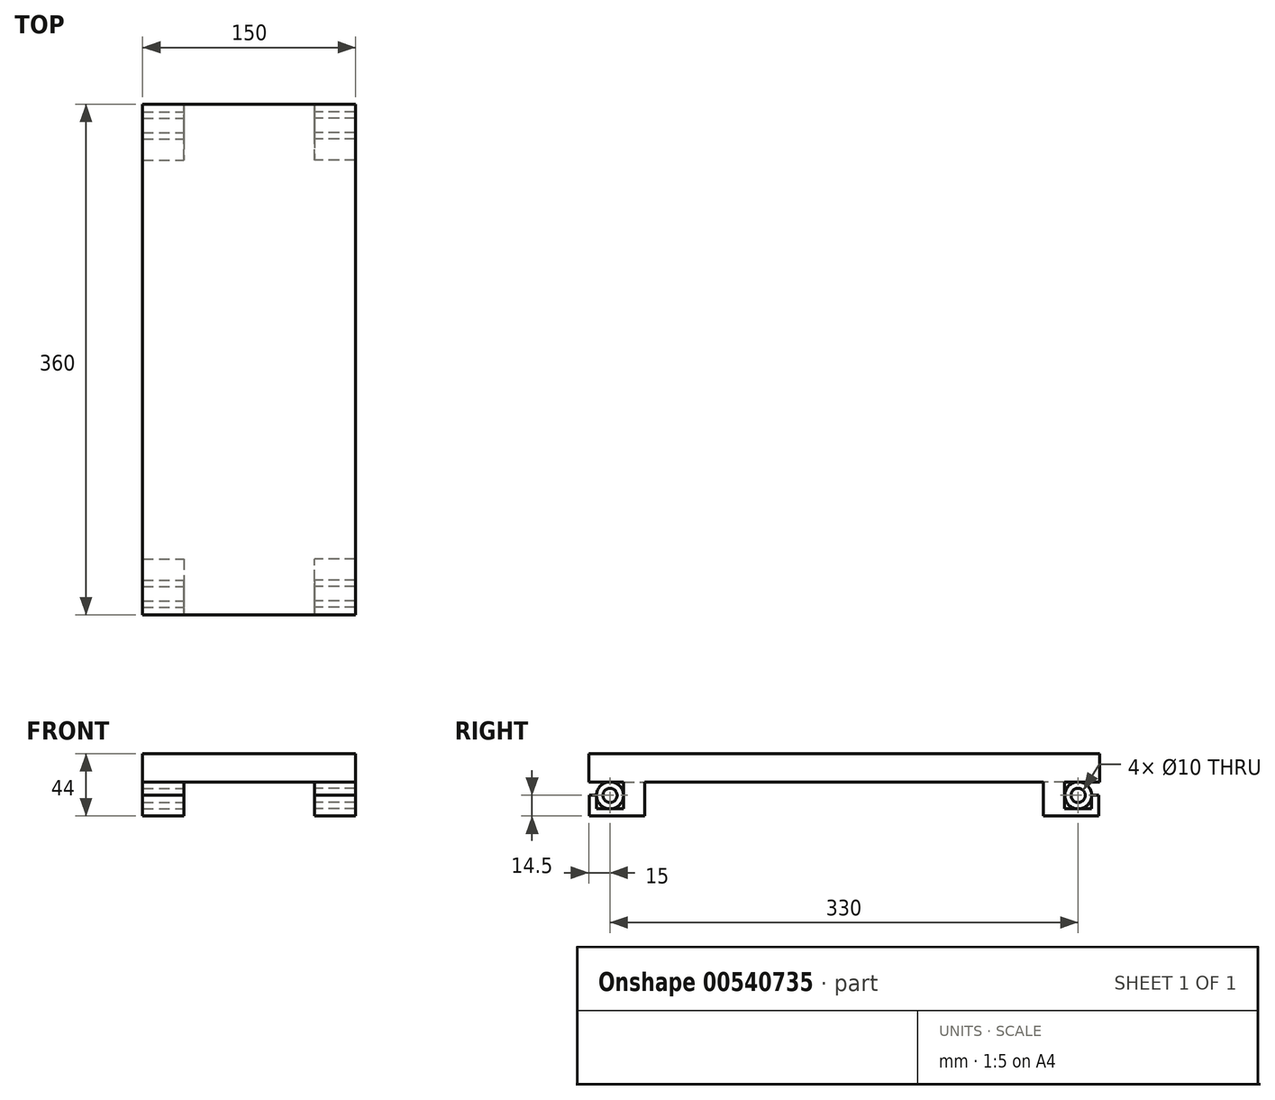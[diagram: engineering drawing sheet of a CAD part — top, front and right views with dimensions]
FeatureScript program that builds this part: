
annotation { "Feature Type Name" : "Feature", "Feature Type Description" : "" }
export const myFeature = defineFeature(function(context is Context, id is Id, definition is map)
    precondition{}
    {
        {
            var Q0;
            Q0=qCreatedBy(makeId("Right.planeOp"),FACE);
            var sketch = newSketch(context, id + "F0", { "sketchPlane" : qUnion([Q0])});
            skLineSegment(sketch, "E0.bottom", {"start": v(-180, 0) * mm, "end": v(180, 0) * mm});
            skLineSegment(sketch, "E0.top", {"start": v(-180, -20) * mm, "end": v(180, -20) * mm});
            skLineSegment(sketch, "E0.left", {"start": v(-180, 0) * mm, "end": v(-180, -20) * mm});
            skLineSegment(sketch, "E0.right", {"start": v(180, 0) * mm, "end": v(180, -20) * mm});
            skCircle(sketch, "E1", {"center": v(-165, -29.5) * mm, "radius": 9.5 * mm});
            skLineSegment(sketch, "E2", {"start": v(-165, -29.5) * mm, "end": v(165, -29.5) * mm, "construction": true});
            skCircle(sketch, "E3", {"center": v(165, -29.5) * mm, "radius": 9.5 * mm});
            skCircle(sketch, "E4", {"center": v(-165, -29.5) * mm, "radius": 5 * mm});
            skCircle(sketch, "E5", {"center": v(165, -29.5) * mm, "radius": 5 * mm});
            skPoint(sketch, "E6", {"position": v(0, 0) * mm});
            skLineSegment(sketch, "E7", {"start": v(-174.5, -29.5) * mm, "end": v(-179.5, -29.5) * mm});
            skLineSegment(sketch, "E8", {"start": v(-179.5, -29.5) * mm, "end": v(-179.5, -44) * mm});
            skLineSegment(sketch, "E9", {"start": v(-179.5, -44) * mm, "end": v(-140.5, -44) * mm});
            skLineSegment(sketch, "E10", {"start": v(-140.5, -44) * mm, "end": v(-140.5, -20) * mm});
            skLineSegment(sketch, "E11", {"start": v(-155.5, -20) * mm, "end": v(-155.5, -39) * mm});
            skLineSegment(sketch, "E12", {"start": v(-155.5, -39) * mm, "end": v(-174.5, -39) * mm});
            skLineSegment(sketch, "E13", {"start": v(-174.5, -39) * mm, "end": v(-174.5, -29.5) * mm});
            skPoint(sketch, "E14", {"position": v(0, -29.5) * mm});
            skLineSegment(sketch, "E15", {"start": v(0, 0) * mm, "end": v(0, -42.12) * mm, "construction": true});
            skLineSegment(sketch, "E16.MirrorCS", {"start": v(140.5, -44) * mm, "end": v(140.5, -20) * mm});
            skLineSegment(sketch, "E17.MirrorCS", {"start": v(155.5, -20) * mm, "end": v(155.5, -39) * mm});
            skLineSegment(sketch, "E18.MirrorCS", {"start": v(155.5, -39) * mm, "end": v(174.5, -39) * mm});
            skLineSegment(sketch, "E19.MirrorCS", {"start": v(179.5, -44) * mm, "end": v(140.5, -44) * mm});
            skLineSegment(sketch, "E20.MirrorCS", {"start": v(174.5, -39) * mm, "end": v(174.5, -29.5) * mm});
            skLineSegment(sketch, "E21.MirrorCS", {"start": v(174.5, -29.5) * mm, "end": v(179.5, -29.5) * mm});
            skLineSegment(sketch, "E22.MirrorCS", {"start": v(179.5, -29.5) * mm, "end": v(179.5, -44) * mm});
            skSolve(sketch);
        }
        {
            var Q0;
            Q0=makeQuery(id+"F0.imprint","IMPRINT",FACE,{"disambiguationData":[TD([[makeQuery(id+"F0.imprint","IMPRINT",EDGE,{"derivedFrom":sQuery(id+"F0.wireOp",EDGE,"E0.bottom")}),-1.0]])]});
            extrude(context, id + "F1", {"entities" : qUnion([Q0]), "endBound" : BoundingType.SYMMETRIC, "depth" : 150 * mm, "offsetDistance" : 25 * mm});
        }
        {
            var Q0;
            Q0=makeQuery(id+"F0.imprint","IMPRINT",FACE,{"disambiguationData":[TD([[makeQuery(id+"F0.imprint","IMPRINT",EDGE,{"derivedFrom":sQuery(id+"F0.wireOp",EDGE,"E7")}),1.0]])]});
            var Q1;
            {var subQ5=sQuery(id+"F0.wireOp",EDGE,"E16.MirrorCS");Q1=makeQuery(id+"F0.imprint","IMPRINT",FACE,{"disambiguationData":[TD([[makeQuery(id+"F0.imprint","IMPRINT",EDGE,{"derivedFrom":subQ5}),-1.0]])]});}
            var Q2;
            Q2=makeQuery(id+"F0.imprint","IMPRINT",FACE,{"disambiguationData":[TD([[makeQuery(id+"F0.imprint","IMPRINT",EDGE,{"derivedFrom":sQuery(id+"F0.wireOp",EDGE,"E4")}),-1.0]])]});
            var Q3;
            Q3=makeQuery(id+"F0.imprint","IMPRINT",FACE,{"disambiguationData":[TD([[makeQuery(id+"F0.imprint","IMPRINT",EDGE,{"derivedFrom":sQuery(id+"F0.wireOp",EDGE,"E5")}),-1.0]])]});
            var Q4;
            Q4=makeQuery(id+"F1.opExtrude","CAP_FACE",FACE,{"disambiguationData":[OSD([sQuery(id+"F0.wireOp",EDGE,"E0.bottom"),sQuery(id+"F0.wireOp",EDGE,"E0.top"),sQuery(id+"F0.wireOp",EDGE,"E0.left"),sQuery(id+"F0.wireOp",EDGE,"E0.right")])],"isStart":false});
            var Q5;
            Q5=makeQuery(id+"F1.opExtrude","CAP_FACE",FACE,{"disambiguationData":[OSD([sQuery(id+"F0.wireOp",EDGE,"E0.bottom"),sQuery(id+"F0.wireOp",EDGE,"E0.top"),sQuery(id+"F0.wireOp",EDGE,"E0.left"),sQuery(id+"F0.wireOp",EDGE,"E0.right")])],"isStart":false});
            extrude(context, id + "F2", {"entities" : qUnion([Q0, Q1, Q2, Q3]), "operationType" : NewBodyOperationType.ADD, "endBound" : BoundingType.UP_TO_SURFACE, "depth" : 25 * mm, "endBoundEntityFace" : qUnion([Q4]), "offsetDistance" : 25 * mm, "hasSecondDirection" : true, "secondDirectionBound" : SecondDirectionBoundingType.UP_TO_SURFACE, "secondDirectionOppositeDirection" : false, "secondDirectionDepth" : 50.3 * mm, "secondDirectionBoundEntityFace" : qUnion([Q5]), "hasSecondDirectionOffset" : true, "secondDirectionOffsetDistance" : 29 * mm});
        }
        {
            var Q0;
            Q0=makeQuery(id+"F0.imprint","IMPRINT",FACE,{"disambiguationData":[TD([[makeQuery(id+"F0.imprint","IMPRINT",EDGE,{"derivedFrom":sQuery(id+"F0.wireOp",EDGE,"E4")}),-1.0]])]});
            var Q1;
            Q1=makeQuery(id+"F0.imprint","IMPRINT",FACE,{"disambiguationData":[TD([[makeQuery(id+"F0.imprint","IMPRINT",EDGE,{"derivedFrom":sQuery(id+"F0.wireOp",EDGE,"E7")}),1.0]])]});
            var Q2;
            Q2=makeQuery(id+"F0.imprint","IMPRINT",FACE,{"disambiguationData":[TD([[makeQuery(id+"F0.imprint","IMPRINT",EDGE,{"derivedFrom":sQuery(id+"F0.wireOp",EDGE,"E5")}),-1.0]])]});
            var Q3;
            {var subQ5=sQuery(id+"F0.wireOp",EDGE,"E16.MirrorCS");Q3=makeQuery(id+"F0.imprint","IMPRINT",FACE,{"disambiguationData":[TD([[makeQuery(id+"F0.imprint","IMPRINT",EDGE,{"derivedFrom":subQ5}),-1.0]])]});}
            var Q4;
            Q4=makeQuery(id+"F1.opExtrude","CAP_FACE",FACE,{"disambiguationData":[OSD([sQuery(id+"F0.wireOp",EDGE,"E0.bottom"),sQuery(id+"F0.wireOp",EDGE,"E0.top"),sQuery(id+"F0.wireOp",EDGE,"E0.left"),sQuery(id+"F0.wireOp",EDGE,"E0.right")])],"isStart":true});
            var Q5;
            Q5=makeQuery(id+"F1.opExtrude","CAP_FACE",FACE,{"disambiguationData":[OSD([sQuery(id+"F0.wireOp",EDGE,"E0.bottom"),sQuery(id+"F0.wireOp",EDGE,"E0.top"),sQuery(id+"F0.wireOp",EDGE,"E0.left"),sQuery(id+"F0.wireOp",EDGE,"E0.right")])],"isStart":true});
            extrude(context, id + "F3", {"entities" : qUnion([Q0, Q1, Q2, Q3]), "operationType" : NewBodyOperationType.ADD, "endBound" : BoundingType.UP_TO_SURFACE, "oppositeDirection" : true, "depth" : 25 * mm, "endBoundEntityFace" : qUnion([Q4]), "offsetDistance" : 25 * mm, "hasSecondDirection" : true, "secondDirectionBound" : SecondDirectionBoundingType.UP_TO_SURFACE, "secondDirectionOppositeDirection" : true, "secondDirectionDepth" : 46.7 * mm, "secondDirectionBoundEntityFace" : qUnion([Q5]), "hasSecondDirectionOffset" : true, "secondDirectionOffsetDistance" : 29 * mm});
        }
    });
